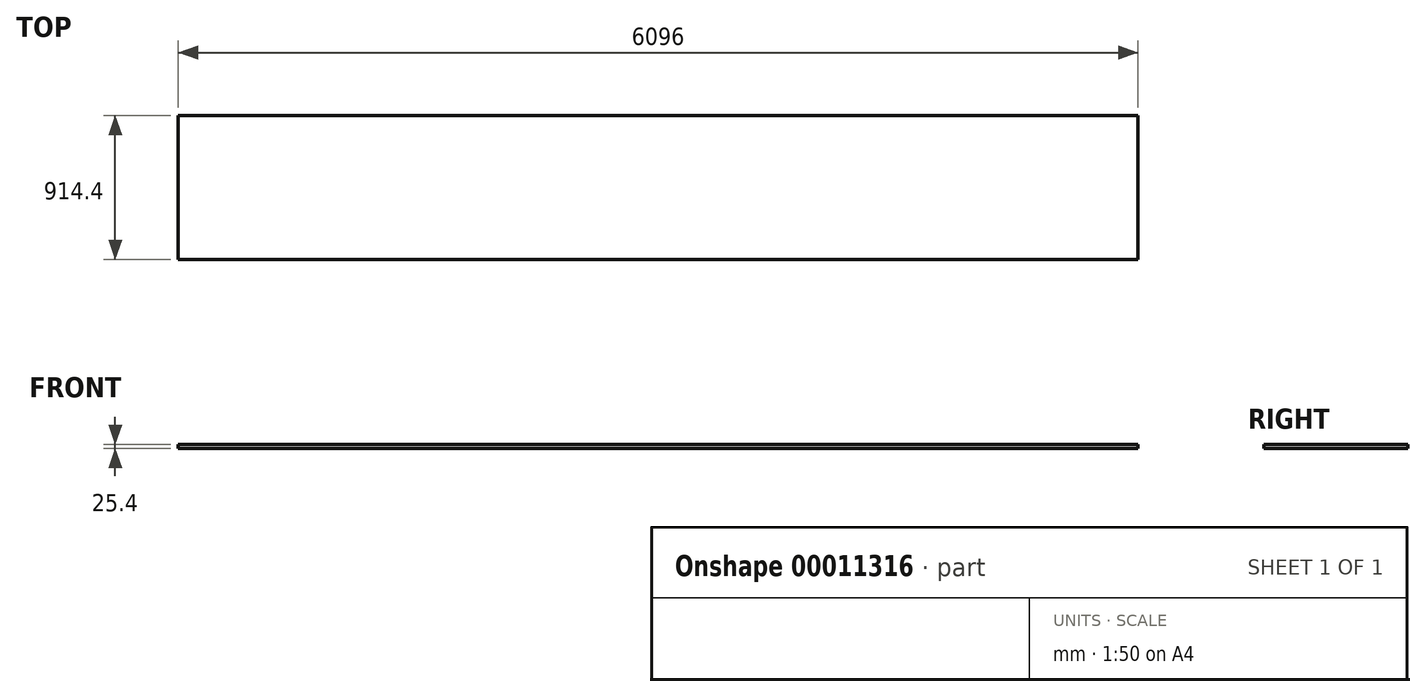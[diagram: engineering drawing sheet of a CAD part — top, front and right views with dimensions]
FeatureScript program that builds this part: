
annotation { "Feature Type Name" : "Feature", "Feature Type Description" : "" }
export const myFeature = defineFeature(function(context is Context, id is Id, definition is map)
    precondition{}
    {
        {
            var Q0;
            Q0=qCreatedBy(makeId("Top.planeOp"),FACE);
            var sketch = newSketch(context, id + "F0", { "sketchPlane" : qUnion([Q0])});
            skLineSegment(sketch, "E0.bottom", {"start": v(0, 457.2) * mm, "end": v(6096, 457.2) * mm});
            skLineSegment(sketch, "E0.top", {"start": v(0, -457.2) * mm, "end": v(6096, -457.2) * mm});
            skLineSegment(sketch, "E0.left", {"start": v(0, 457.2) * mm, "end": v(0, -457.2) * mm});
            skLineSegment(sketch, "E0.right", {"start": v(6096, 457.2) * mm, "end": v(6096, -457.2) * mm});
            skSolve(sketch);
        }
        {
            var Q0;
            Q0=makeQuery(id+"F0.imprint","IMPRINT",FACE,{"disambiguationData":[TD([[makeQuery(id+"F0.imprint","IMPRINT",EDGE,{"derivedFrom":sQuery(id+"F0.wireOp",EDGE,"E0.bottom")}),-1.0]])]});
            extrude(context, id + "F1", {"entities" : qUnion([Q0]), "depth" : 25.4 * mm});
        }
    });
